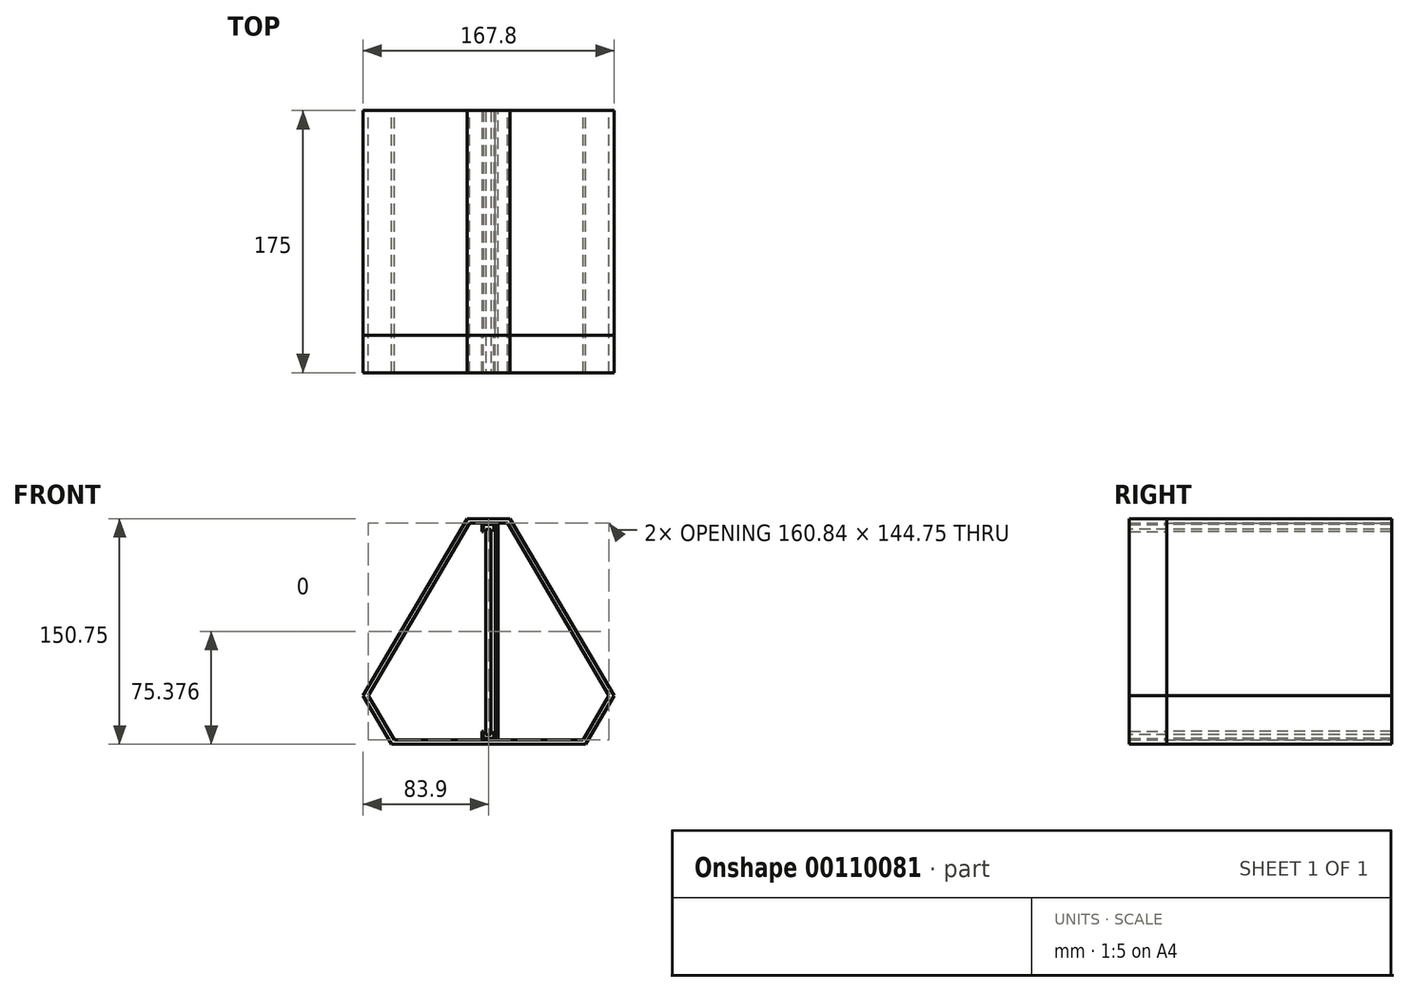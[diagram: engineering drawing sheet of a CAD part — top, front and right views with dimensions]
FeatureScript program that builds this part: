
annotation { "Feature Type Name" : "Feature", "Feature Type Description" : "" }
export const myFeature = defineFeature(function(context is Context, id is Id, definition is map)
    precondition{}
    {
        {
            var Q0;
            Q0=qCreatedBy(makeId("Front.planeOp"),FACE);
            var sketch = newSketch(context, id + "F0", { "sketchPlane" : qUnion([Q0])});
            skLineSegment(sketch, "E0", {"start": v(-63.04, 0) * mm, "end": v(63.04, 0) * mm});
            skLineSegment(sketch, "E1", {"start": v(0, 0) * mm, "end": v(0, 166.28) * mm, "construction": true});
            skLineSegment(sketch, "E2", {"start": v(-80.42, 29.55) * mm, "end": v(-12.66, 144.75) * mm});
            skLineSegment(sketch, "E3", {"start": v(12.66, 144.75) * mm, "end": v(80.42, 29.55) * mm});
            skLineSegment(sketch, "E4", {"start": v(-12.66, 144.75) * mm, "end": v(12.66, 144.75) * mm});
            skLineSegment(sketch, "E5", {"start": v(-80.42, 29.55) * mm, "end": v(-80.42, 0) * mm, "construction": true});
            skLineSegment(sketch, "E6.MirrorCS", {"start": v(-63.04, 0) * mm, "end": v(-80.42, 29.55) * mm});
            skPoint(sketch, "E7.orphan", {"position": v(-148.18, 144.75) * mm});
            skPoint(sketch, "E8.orphan", {"position": v(-97.8, 0) * mm});
            skLineSegment(sketch, "E9.MirrorCS", {"start": v(63.04, 0) * mm, "end": v(80.42, 29.55) * mm});
            skLineSegment(sketch, "E10.0", {"start": v(-64.76, -3) * mm, "end": v(-83.9, 29.55) * mm});
            skLineSegment(sketch, "E10.1", {"start": v(-14.38, 147.75) * mm, "end": v(14.38, 147.75) * mm});
            skLineSegment(sketch, "E10.2", {"start": v(14.38, 147.75) * mm, "end": v(83.9, 29.55) * mm});
            skLineSegment(sketch, "E10.3", {"start": v(-83.9, 29.55) * mm, "end": v(-14.38, 147.75) * mm});
            skLineSegment(sketch, "E10.4", {"start": v(64.76, -3) * mm, "end": v(83.9, 29.55) * mm});
            skLineSegment(sketch, "E10.5", {"start": v(-64.76, -3) * mm, "end": v(64.76, -3) * mm});
            skSolve(sketch);
        }
        {
            var Q0;
            Q0=makeQuery(id+"F0.imprint","IMPRINT",FACE,{"disambiguationData":[TD([[makeQuery(id+"F0.imprint","IMPRINT",EDGE,{"derivedFrom":sQuery(id+"F0.wireOp",EDGE,"E0")}),-1.0]])]});
            extrude(context, id + "F1", {"entities" : qUnion([Q0]), "depth" : 150 * mm});
        }
        {
            var Q0;
            Q0=makeQuery(id+"F1.opExtrude","CAP_FACE",FACE,{"disambiguationData":[OSD([sQuery(id+"F0.wireOp",EDGE,"E0"),sQuery(id+"F0.wireOp",EDGE,"E2"),sQuery(id+"F0.wireOp",EDGE,"E3"),sQuery(id+"F0.wireOp",EDGE,"E4"),sQuery(id+"F0.wireOp",EDGE,"E6.MirrorCS"),sQuery(id+"F0.wireOp",EDGE,"E9.MirrorCS"),sQuery(id+"F0.wireOp",EDGE,"E10.0"),sQuery(id+"F0.wireOp",EDGE,"E10.1"),sQuery(id+"F0.wireOp",EDGE,"E10.2"),sQuery(id+"F0.wireOp",EDGE,"E10.3"),sQuery(id+"F0.wireOp",EDGE,"E10.4"),sQuery(id+"F0.wireOp",EDGE,"E10.5")])],"isStart":false});
            var sketch = newSketch(context, id + "F2", { "sketchPlane" : qUnion([Q0])});
            skLineSegment(sketch, "E11", {"start": v(-4.43, 5.71) * mm, "end": v(-4.43, 0) * mm});
            skLineSegment(sketch, "E12", {"start": v(-4.43, 0) * mm, "end": v(0, 0) * mm});
            skLineSegment(sketch, "E13", {"start": v(0, 0) * mm, "end": v(0, 1.08) * mm});
            skLineSegment(sketch, "E14", {"start": v(0, 1.08) * mm, "end": v(-3.4, 1.08) * mm});
            skLineSegment(sketch, "E15", {"start": v(-3.4, 1.08) * mm, "end": v(-3.4, 5.71) * mm});
            skLineSegment(sketch, "E16", {"start": v(-3.4, 5.71) * mm, "end": v(-4.43, 5.71) * mm});
            skLineSegment(sketch, "E17.MirrorCS", {"start": v(3.4, 5.71) * mm, "end": v(4.43, 5.71) * mm});
            skLineSegment(sketch, "E18.MirrorCS", {"start": v(4.43, 5.71) * mm, "end": v(4.43, 0) * mm});
            skLineSegment(sketch, "E19.MirrorCS", {"start": v(3.4, 1.08) * mm, "end": v(3.4, 5.71) * mm});
            skLineSegment(sketch, "E20.MirrorCS", {"start": v(0, 1.08) * mm, "end": v(3.4, 1.08) * mm});
            skLineSegment(sketch, "E21.MirrorCS", {"start": v(4.43, 0) * mm, "end": v(0, 0) * mm});
            skPoint(sketch, "E22.orphan", {"position": v(-9.84, 5.71) * mm});
            skPoint(sketch, "E23.orphan", {"position": v(9.84, 5.71) * mm});
            skLineSegment(sketch, "E24", {"start": v(0, 144.75) * mm, "end": v(0, 0) * mm, "construction": true});
            skLineSegment(sketch, "E25", {"start": v(0, 72.38) * mm, "end": v(-93.7, 72.38) * mm, "construction": true});
            skLineSegment(sketch, "E26.MirrorCS", {"start": v(-3.4, 139.04) * mm, "end": v(-4.43, 139.04) * mm});
            skLineSegment(sketch, "E27.MirrorCS", {"start": v(-4.43, 139.04) * mm, "end": v(-4.43, 144.75) * mm});
            skLineSegment(sketch, "E28.MirrorCS", {"start": v(-3.4, 143.68) * mm, "end": v(-3.4, 139.04) * mm});
            skLineSegment(sketch, "E29.MirrorCS", {"start": v(0, 143.68) * mm, "end": v(-3.4, 143.68) * mm});
            skLineSegment(sketch, "E30.MirrorCS", {"start": v(-4.43, 144.75) * mm, "end": v(0, 144.75) * mm});
            skLineSegment(sketch, "E31.MirrorCS", {"start": v(4.43, 144.75) * mm, "end": v(0, 144.75) * mm});
            skLineSegment(sketch, "E32.MirrorCS", {"start": v(0, 143.68) * mm, "end": v(3.4, 143.68) * mm});
            skLineSegment(sketch, "E33.MirrorCS", {"start": v(3.4, 143.68) * mm, "end": v(3.4, 139.04) * mm});
            skLineSegment(sketch, "E34.MirrorCS", {"start": v(3.4, 139.04) * mm, "end": v(4.43, 139.04) * mm});
            skLineSegment(sketch, "E35.MirrorCS", {"start": v(4.43, 139.04) * mm, "end": v(4.43, 144.75) * mm});
            skSolve(sketch);
        }
        {
            var Q0;
            {var subQ0=sQuery(id+"F2.wireOp",EDGE,"E11");Q0=makeQuery(id+"F2.imprint","IMPRINT",FACE,{"disambiguationData":[TD([[makeQuery(id+"F2.imprint","IMPRINT",EDGE,{"derivedFrom":subQ0}),1.0]])]});}
            var Q1;
            Q1=makeQuery(id+"F2.imprint","IMPRINT",FACE,{"disambiguationData":[TD([[makeQuery(id+"F2.imprint","IMPRINT",EDGE,{"derivedFrom":sQuery(id+"F2.wireOp",EDGE,"E13")}),-1.0]])]});
            var Q2;
            Q2=makeQuery(id+"F2.imprint","IMPRINT",FACE,{"disambiguationData":[TD([[makeQuery(id+"F2.imprint","IMPRINT",EDGE,{"derivedFrom":sQuery(id+"F2.wireOp",EDGE,"E26.MirrorCS")}),-1.0]])]});
            extrude(context, id + "F3", {"entities" : qUnion([Q0, Q1, Q2]), "oppositeDirection" : true, "depth" : 150 * mm});
        }
        {
            var Q0;
            Q0=makeQuery(id+"F3.boolean.opBoolean","MERGE",FACE,{"derivedFrom":[makeQuery(id+"F1.opExtrude","CAP_FACE",FACE,{"disambiguationData":[OSD([sQuery(id+"F0.wireOp",EDGE,"E0"),sQuery(id+"F0.wireOp",EDGE,"E2"),sQuery(id+"F0.wireOp",EDGE,"E3"),sQuery(id+"F0.wireOp",EDGE,"E4"),sQuery(id+"F0.wireOp",EDGE,"E6.MirrorCS"),sQuery(id+"F0.wireOp",EDGE,"E9.MirrorCS"),sQuery(id+"F0.wireOp",EDGE,"E10.0"),sQuery(id+"F0.wireOp",EDGE,"E10.1"),sQuery(id+"F0.wireOp",EDGE,"E10.2"),sQuery(id+"F0.wireOp",EDGE,"E10.3"),sQuery(id+"F0.wireOp",EDGE,"E10.4"),sQuery(id+"F0.wireOp",EDGE,"E10.5")])],"isStart":false}),makeQuery(id+"F3.opExtrude","CAP_FACE",FACE,{"disambiguationData":[OSD([sQuery(id+"F2.wireOp",EDGE,"E11"),sQuery(id+"F2.wireOp",EDGE,"E12"),sQuery(id+"F2.wireOp",EDGE,"E14"),sQuery(id+"F2.wireOp",EDGE,"E15"),sQuery(id+"F2.wireOp",EDGE,"E16"),sQuery(id+"F2.wireOp",EDGE,"E17.MirrorCS"),sQuery(id+"F2.wireOp",EDGE,"E18.MirrorCS"),sQuery(id+"F2.wireOp",EDGE,"E19.MirrorCS"),sQuery(id+"F2.wireOp",EDGE,"E20.MirrorCS"),sQuery(id+"F2.wireOp",EDGE,"E21.MirrorCS")])],"isStart":true}),makeQuery(id+"F3.opExtrude","CAP_FACE",FACE,{"disambiguationData":[OSD([sQuery(id+"F2.wireOp",EDGE,"E26.MirrorCS"),sQuery(id+"F2.wireOp",EDGE,"E27.MirrorCS"),sQuery(id+"F2.wireOp",EDGE,"E28.MirrorCS"),sQuery(id+"F2.wireOp",EDGE,"E29.MirrorCS"),sQuery(id+"F2.wireOp",EDGE,"E30.MirrorCS"),sQuery(id+"F2.wireOp",EDGE,"E31.MirrorCS"),sQuery(id+"F2.wireOp",EDGE,"E32.MirrorCS"),sQuery(id+"F2.wireOp",EDGE,"E33.MirrorCS"),sQuery(id+"F2.wireOp",EDGE,"E34.MirrorCS"),sQuery(id+"F2.wireOp",EDGE,"E35.MirrorCS")])],"isStart":true})]});
            extrude(context, id + "F4", {"entities" : qUnion([Q0]), "depth" : 25 * mm});
        }
        {
            var Q0;
            Q0=makeQuery(id+"F4.opExtrude","CAP_FACE",FACE,{"disambiguationData":[OSD([sQuery(id+"F0.wireOp",EDGE,"E0"),sQuery(id+"F0.wireOp",EDGE,"E2"),sQuery(id+"F0.wireOp",EDGE,"E3"),sQuery(id+"F0.wireOp",EDGE,"E4"),sQuery(id+"F0.wireOp",EDGE,"E6.MirrorCS"),sQuery(id+"F0.wireOp",EDGE,"E9.MirrorCS"),sQuery(id+"F0.wireOp",EDGE,"E10.0"),sQuery(id+"F0.wireOp",EDGE,"E10.1"),sQuery(id+"F0.wireOp",EDGE,"E10.2"),sQuery(id+"F0.wireOp",EDGE,"E10.3"),sQuery(id+"F0.wireOp",EDGE,"E10.4"),sQuery(id+"F0.wireOp",EDGE,"E10.5"),sQuery(id+"F2.wireOp",EDGE,"E11"),sQuery(id+"F2.wireOp",EDGE,"E12"),sQuery(id+"F2.wireOp",EDGE,"E14"),sQuery(id+"F2.wireOp",EDGE,"E15"),sQuery(id+"F2.wireOp",EDGE,"E16"),sQuery(id+"F2.wireOp",EDGE,"E17.MirrorCS"),sQuery(id+"F2.wireOp",EDGE,"E18.MirrorCS"),sQuery(id+"F2.wireOp",EDGE,"E19.MirrorCS"),sQuery(id+"F2.wireOp",EDGE,"E20.MirrorCS"),sQuery(id+"F2.wireOp",EDGE,"E21.MirrorCS"),sQuery(id+"F2.wireOp",EDGE,"E26.MirrorCS"),sQuery(id+"F2.wireOp",EDGE,"E27.MirrorCS"),sQuery(id+"F2.wireOp",EDGE,"E28.MirrorCS"),sQuery(id+"F2.wireOp",EDGE,"E29.MirrorCS"),sQuery(id+"F2.wireOp",EDGE,"E30.MirrorCS"),sQuery(id+"F2.wireOp",EDGE,"E31.MirrorCS"),sQuery(id+"F2.wireOp",EDGE,"E32.MirrorCS"),sQuery(id+"F2.wireOp",EDGE,"E33.MirrorCS"),sQuery(id+"F2.wireOp",EDGE,"E34.MirrorCS"),sQuery(id+"F2.wireOp",EDGE,"E35.MirrorCS")])],"isStart":false});
            var sketch = newSketch(context, id + "F5", { "sketchPlane" : qUnion([Q0])});
            skPoint(sketch, "E36.oppositeSnap0", {"position": v(3.4, 3.4) * mm});
            skLineSegment(sketch, "E36.bottom", {"start": v(-1.8, 140.78) * mm, "end": v(1.61, 140.78) * mm});
            skLineSegment(sketch, "E36.top", {"start": v(-1.8, 3.4) * mm, "end": v(1.61, 3.4) * mm});
            skLineSegment(sketch, "E36.left", {"start": v(-1.8, 140.78) * mm, "end": v(-1.8, 3.4) * mm});
            skLineSegment(sketch, "E36.right", {"start": v(1.61, 140.78) * mm, "end": v(1.61, 3.4) * mm});
            skSolve(sketch);
        }
        {
            var Q0;
            Q0=qSketchRegion(id+"F5",true);
            extrude(context, id + "F6", {"entities" : qUnion([Q0]), "oppositeDirection" : true, "depth" : 175 * mm});
        }
        {
            var Q0;
            Q0=makeQuery(id+"F1.opExtrude","CAP_FACE",FACE,{"disambiguationData":[OSD([sQuery(id+"F0.wireOp",EDGE,"E0"),sQuery(id+"F0.wireOp",EDGE,"E2"),sQuery(id+"F0.wireOp",EDGE,"E3"),sQuery(id+"F0.wireOp",EDGE,"E4"),sQuery(id+"F0.wireOp",EDGE,"E6.MirrorCS"),sQuery(id+"F0.wireOp",EDGE,"E9.MirrorCS"),sQuery(id+"F0.wireOp",EDGE,"E10.0"),sQuery(id+"F0.wireOp",EDGE,"E10.1"),sQuery(id+"F0.wireOp",EDGE,"E10.2"),sQuery(id+"F0.wireOp",EDGE,"E10.3"),sQuery(id+"F0.wireOp",EDGE,"E10.4"),sQuery(id+"F0.wireOp",EDGE,"E10.5")])],"isStart":true});
            var sketch = newSketch(context, id + "F7", { "sketchPlane" : qUnion([Q0])});
            skLineSegment(sketch, "E37.bottom", {"start": v(-4.43, 144.75) * mm, "end": v(-6.43, 144.75) * mm});
            skLineSegment(sketch, "E37.top", {"start": v(-4.43, 0) * mm, "end": v(-6.43, 0) * mm});
            skLineSegment(sketch, "E37.left", {"start": v(-4.43, 144.75) * mm, "end": v(-4.43, 0) * mm});
            skLineSegment(sketch, "E37.right", {"start": v(-6.43, 144.75) * mm, "end": v(-6.43, 0) * mm});
            skSolve(sketch);
        }
        {
            var Q0;
            Q0=qSketchRegion(id+"F7",true);
            var Q1;
            Q1=makeQuery(id+"F4.opExtrude","CAP_FACE",FACE,{"disambiguationData":[OSD([sQuery(id+"F0.wireOp",EDGE,"E0"),sQuery(id+"F0.wireOp",EDGE,"E2"),sQuery(id+"F0.wireOp",EDGE,"E3"),sQuery(id+"F0.wireOp",EDGE,"E4"),sQuery(id+"F0.wireOp",EDGE,"E6.MirrorCS"),sQuery(id+"F0.wireOp",EDGE,"E9.MirrorCS"),sQuery(id+"F0.wireOp",EDGE,"E10.0"),sQuery(id+"F0.wireOp",EDGE,"E10.1"),sQuery(id+"F0.wireOp",EDGE,"E10.2"),sQuery(id+"F0.wireOp",EDGE,"E10.3"),sQuery(id+"F0.wireOp",EDGE,"E10.4"),sQuery(id+"F0.wireOp",EDGE,"E10.5")])],"isStart":false});
            extrude(context, id + "F8", {"entities" : qUnion([Q0]), "endBound" : BoundingType.UP_TO_SURFACE, "oppositeDirection" : true, "endBoundEntityFace" : qUnion([Q1]), "depth" : 25 * mm});
        }
    });
